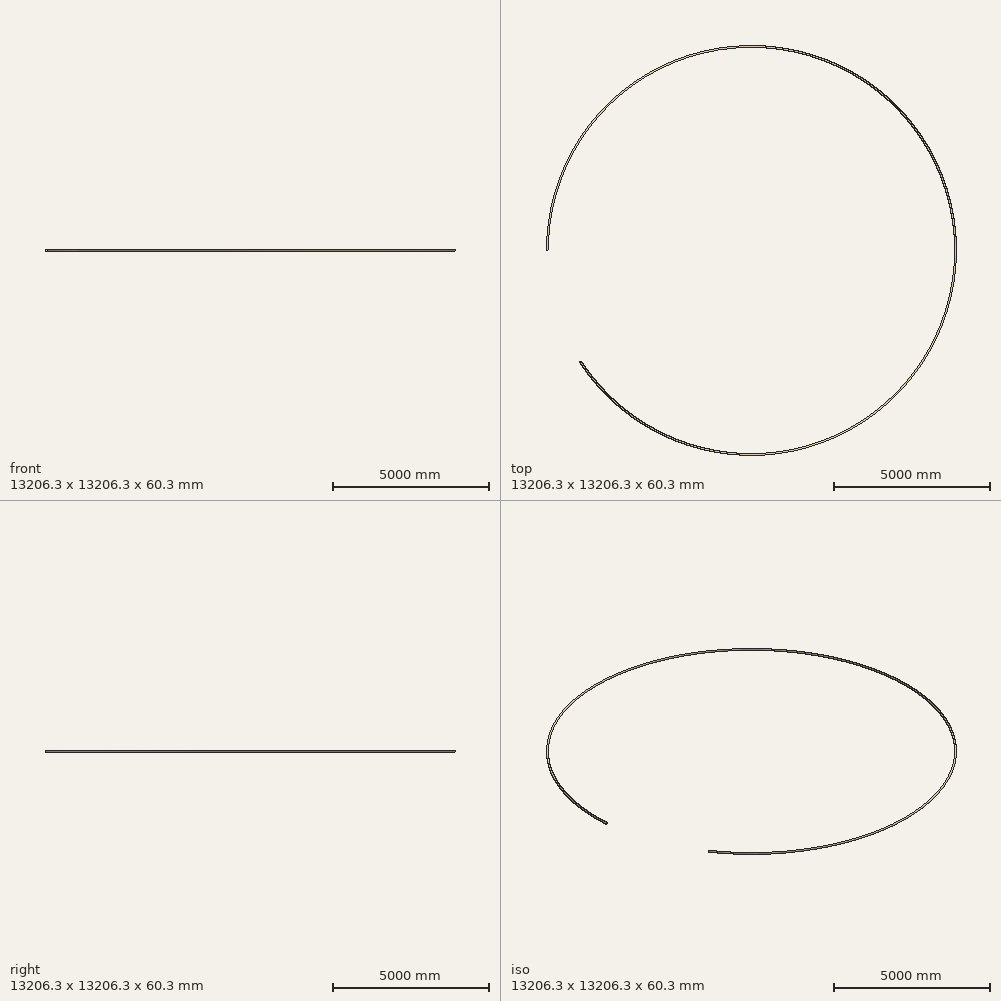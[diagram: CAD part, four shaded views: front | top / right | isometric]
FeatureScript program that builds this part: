
annotation { "Feature Type Name" : "Feature", "Feature Type Description" : "" }
export const myFeature = defineFeature(function(context is Context, id is Id, definition is map)
    precondition{}
    {
        {
            var Q0;
            Q0=qCreatedBy(makeId("Front.planeOp"),FACE);
            var sketch = newSketch(context, id + "F0", { "sketchPlane" : qUnion([Q0])});
            skCircle(sketch, "E0", {"center": v(0, 0) * mm, "radius": 30.16 * mm});
            skLineSegment(sketch, "E1", {"start": v(0, 0) * mm, "end": v(6573, 0) * mm, "construction": true});
            skLineSegment(sketch, "E2", {"start": v(6573, 0) * mm, "end": v(6573, -100) * mm, "construction": true});
            skCircle(sketch, "E3.0", {"center": v(0, 0) * mm, "radius": 27.4 * mm});
            skSolve(sketch);
        }
        {
            var Q0;
            Q0 = qSketchRegion(id + "F0", true);
            var Q1;
            Q1=sQuery(id+"F0.wireOp",EDGE,"E2");
            revolve(context, id + "F1", {"surfaceOperationType" : NewSurfaceOperationType.NEW, "entities" : qUnion([Q0]), "axis" : qUnion([Q1]), "revolveType" : RevolveType.ONE_DIRECTION, "angle" : 327 * degree});
        }
    });
